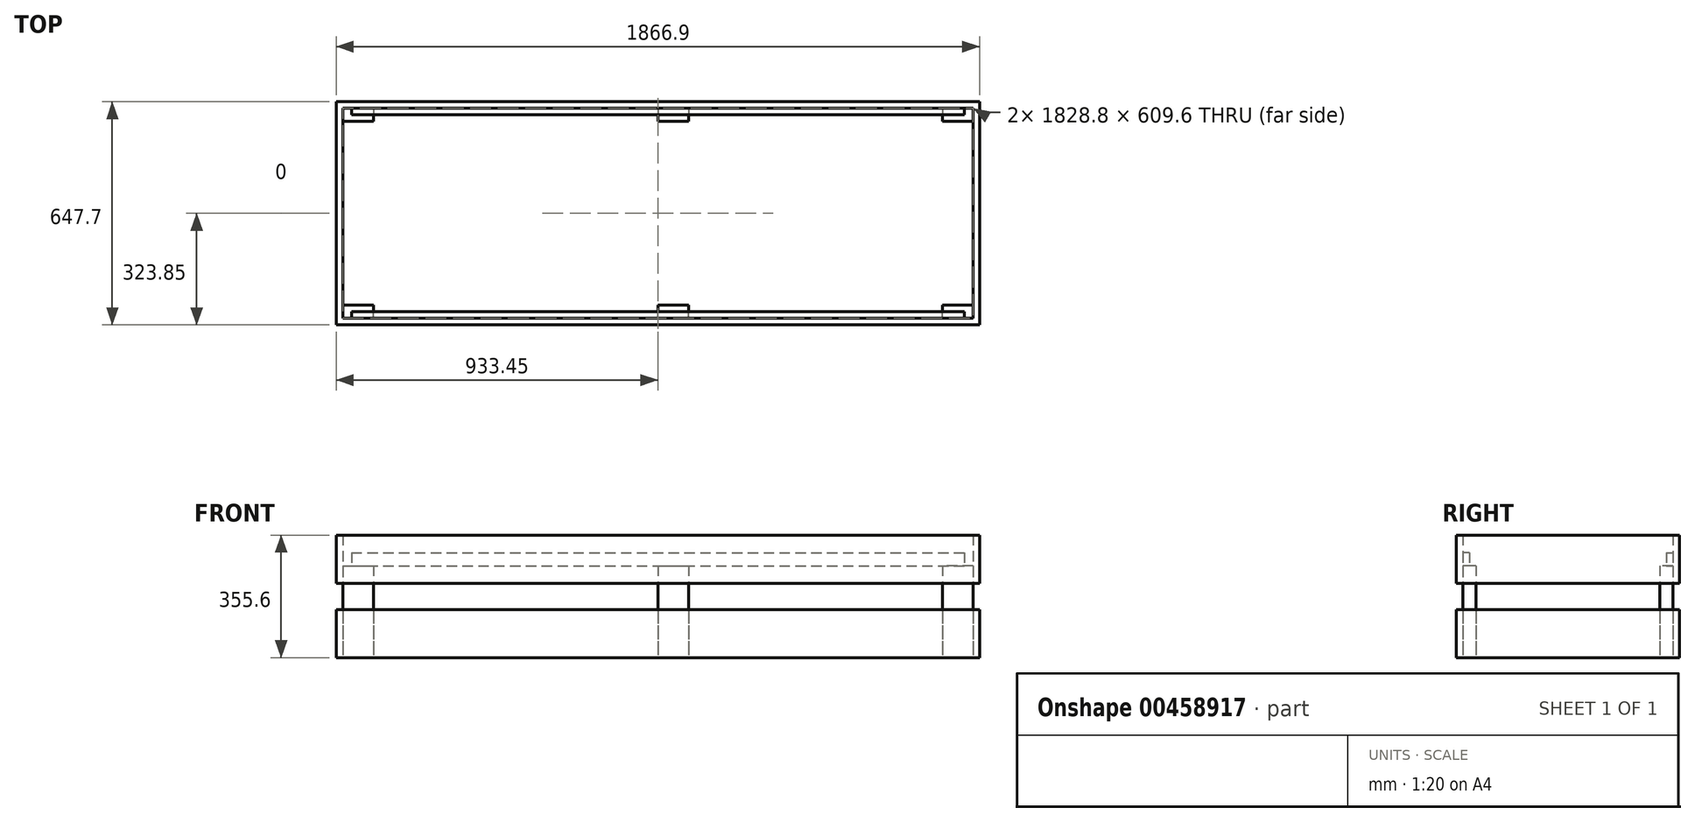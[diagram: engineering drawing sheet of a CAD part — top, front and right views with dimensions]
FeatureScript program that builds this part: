
annotation { "Feature Type Name" : "Feature", "Feature Type Description" : "" }
export const myFeature = defineFeature(function(context is Context, id is Id, definition is map)
    precondition{}
    {
        {
            var Q0;
            Q0=qCreatedBy(makeId("Top.planeOp"),FACE);
            var sketch = newSketch(context, id + "F0", { "sketchPlane" : qUnion([Q0])});
            skLineSegment(sketch, "E0.bottom", {"start": v(-933.45, 323.85) * mm, "end": v(933.45, 323.85) * mm});
            skLineSegment(sketch, "E0.top", {"start": v(-933.45, -323.85) * mm, "end": v(933.45, -323.85) * mm});
            skLineSegment(sketch, "E0.left", {"start": v(-933.45, 323.85) * mm, "end": v(-933.45, -323.85) * mm});
            skLineSegment(sketch, "E0.right", {"start": v(933.45, 323.85) * mm, "end": v(933.45, -323.85) * mm});
            skLineSegment(sketch, "E1", {"start": v(-933.45, 323.85) * mm, "end": v(933.45, -323.85) * mm, "construction": true});
            skSolve(sketch);
        }
        {
            var Q0;
            Q0=makeQuery(id+"F0.imprint","IMPRINT",FACE,{"disambiguationData":[TD([[makeQuery(id+"F0.imprint","IMPRINT",EDGE,{"derivedFrom":sQuery(id+"F0.wireOp",EDGE,"E0.bottom")}),-1.0]])]});
            extrude(context, id + "F1", {"entities" : qUnion([Q0]), "depth" : 355.6 * mm});
        }
        {
            var Q0;
            Q0=makeQuery(id+"F1.opExtrude","CAP_FACE",FACE,{"disambiguationData":[OSD([sQuery(id+"F0.wireOp",EDGE,"E0.bottom"),sQuery(id+"F0.wireOp",EDGE,"E0.top"),sQuery(id+"F0.wireOp",EDGE,"E0.left"),sQuery(id+"F0.wireOp",EDGE,"E0.right")])],"isStart":false});
            var Q1;
            Q1=makeQuery(id+"F1.opExtrude","CAP_FACE",FACE,{"disambiguationData":[OSD([sQuery(id+"F0.wireOp",EDGE,"E0.bottom"),sQuery(id+"F0.wireOp",EDGE,"E0.top"),sQuery(id+"F0.wireOp",EDGE,"E0.left"),sQuery(id+"F0.wireOp",EDGE,"E0.right")])],"isStart":true});
            shell(context, id + "F2", {"entities" : qUnion([Q0, Q1]), "thickness" : 19.05 * mm});
        }
        {
            var Q0;
            Q0=makeQuery(id+"F2.opShell","OFFSET_FACE",FACE,{"disambiguationData":[OSD([sQuery(id+"F0.wireOp",EDGE,"E0.bottom")])]});
            var sketch = newSketch(context, id + "F3", { "sketchPlane" : qUnion([Q0])});
            skLineSegment(sketch, "E2.bottom", {"start": v(-889, 304.8) * mm, "end": v(889, 304.8) * mm});
            skLineSegment(sketch, "E2.top", {"start": v(-889, 266.7) * mm, "end": v(889, 266.7) * mm});
            skLineSegment(sketch, "E2.left", {"start": v(-889, 304.8) * mm, "end": v(-889, 266.7) * mm});
            skLineSegment(sketch, "E2.right", {"start": v(889, 304.8) * mm, "end": v(889, 266.7) * mm});
            skSolve(sketch);
        }
        {
            var Q0;
            Q0=makeQuery(id+"F3.imprint","IMPRINT",FACE,{"disambiguationData":[TD([[makeQuery(id+"F3.imprint","IMPRINT",EDGE,{"derivedFrom":sQuery(id+"F3.wireOp",EDGE,"E2.bottom")}),-1.0]])]});
            extrude(context, id + "F4", {"entities" : qUnion([Q0]), "depth" : 19.05 * mm});
        }
        {
            var Q0;
            Q0=makeQuery(id+"F2.opShell","OFFSET_FACE",FACE,{"disambiguationData":[OSD([sQuery(id+"F0.wireOp",EDGE,"E0.top")])]});
            var sketch = newSketch(context, id + "F5", { "sketchPlane" : qUnion([Q0])});
            skLineSegment(sketch, "E3.bottom", {"start": v(-889, 304.8) * mm, "end": v(889, 304.8) * mm});
            skLineSegment(sketch, "E3.top", {"start": v(-889, 266.7) * mm, "end": v(889, 266.7) * mm});
            skLineSegment(sketch, "E3.left", {"start": v(-889, 304.8) * mm, "end": v(-889, 266.7) * mm});
            skLineSegment(sketch, "E3.right", {"start": v(889, 304.8) * mm, "end": v(889, 266.7) * mm});
            skSolve(sketch);
        }
        {
            var Q0;
            Q0 = qSketchRegion(id + "F5", true);
            extrude(context, id + "F6", {"entities" : qUnion([Q0]), "operationType" : NewBodyOperationType.ADD, "depth" : 19.05 * mm});
        }
        {
            var Q0;
            Q0=makeQuery(id+"F1.opExtrude","SWEPT_FACE",FACE,{"disambiguationData":[OSD([sQuery(id+"F0.wireOp",EDGE,"E0.top")])]});
            var sketch = newSketch(context, id + "F7", { "sketchPlane" : qUnion([Q0])});
            skLineSegment(sketch, "E4.bottom", {"start": v(-933.45, 215.9) * mm, "end": v(933.45, 215.9) * mm});
            skLineSegment(sketch, "E4.top", {"start": v(-933.45, 139.7) * mm, "end": v(933.45, 139.7) * mm});
            skLineSegment(sketch, "E4.left", {"start": v(-933.45, 215.9) * mm, "end": v(-933.45, 139.7) * mm});
            skLineSegment(sketch, "E4.right", {"start": v(933.45, 215.9) * mm, "end": v(933.45, 139.7) * mm});
            skSolve(sketch);
        }
        {
            var Q0;
            Q0=makeQuery(id+"F7.imprint","IMPRINT",FACE,{"disambiguationData":[TD([[makeQuery(id+"F7.imprint","IMPRINT",EDGE,{"derivedFrom":sQuery(id+"F7.wireOp",EDGE,"E4.bottom")}),-1.0]])]});
            extrude(context, id + "F8", {"entities" : qUnion([Q0]), "operationType" : NewBodyOperationType.REMOVE, "endBound" : BoundingType.THROUGH_ALL, "oppositeDirection" : true, "depth" : 25.4 * mm});
        }
        {
            var Q0;
            Q0=makeQuery(id+"F1.opExtrude","CAP_FACE",FACE,{"disambiguationData":[OSD([sQuery(id+"F0.wireOp",EDGE,"E0.bottom"),sQuery(id+"F0.wireOp",EDGE,"E0.top"),sQuery(id+"F0.wireOp",EDGE,"E0.left"),sQuery(id+"F0.wireOp",EDGE,"E0.right")])],"isStart":true});
            var sketch = newSketch(context, id + "F9", { "sketchPlane" : qUnion([Q0])});
            skLineSegment(sketch, "E5.bottom", {"start": v(914.4, -304.8) * mm, "end": v(825.5, -304.8) * mm});
            skLineSegment(sketch, "E5.top", {"start": v(914.4, -266.7) * mm, "end": v(825.5, -266.7) * mm});
            skLineSegment(sketch, "E5.left", {"start": v(914.4, -304.8) * mm, "end": v(914.4, -266.7) * mm});
            skLineSegment(sketch, "E5.right", {"start": v(825.5, -304.8) * mm, "end": v(825.5, -266.7) * mm});
            skLineSegment(sketch, "E6.bottom", {"start": v(914.4, 304.8) * mm, "end": v(825.5, 304.8) * mm});
            skLineSegment(sketch, "E6.top", {"start": v(914.4, 266.7) * mm, "end": v(825.5, 266.7) * mm});
            skLineSegment(sketch, "E6.left", {"start": v(914.4, 304.8) * mm, "end": v(914.4, 266.7) * mm});
            skLineSegment(sketch, "E6.right", {"start": v(825.5, 304.8) * mm, "end": v(825.5, 266.7) * mm});
            skLineSegment(sketch, "E7.bottom", {"start": v(-914.4, -304.8) * mm, "end": v(-825.5, -304.8) * mm});
            skLineSegment(sketch, "E7.top", {"start": v(-914.4, -266.7) * mm, "end": v(-825.5, -266.7) * mm});
            skLineSegment(sketch, "E7.left", {"start": v(-914.4, -304.8) * mm, "end": v(-914.4, -266.7) * mm});
            skLineSegment(sketch, "E7.right", {"start": v(-825.5, -304.8) * mm, "end": v(-825.5, -266.7) * mm});
            skLineSegment(sketch, "E8.bottom", {"start": v(-914.4, 304.8) * mm, "end": v(-825.5, 304.8) * mm});
            skLineSegment(sketch, "E8.top", {"start": v(-914.4, 266.7) * mm, "end": v(-825.5, 266.7) * mm});
            skLineSegment(sketch, "E8.left", {"start": v(-914.4, 304.8) * mm, "end": v(-914.4, 266.7) * mm});
            skLineSegment(sketch, "E8.right", {"start": v(-825.5, 304.8) * mm, "end": v(-825.5, 266.7) * mm});
            skLineSegment(sketch, "E9.bottom", {"start": v(88.9, 304.8) * mm, "end": v(0, 304.8) * mm});
            skLineSegment(sketch, "E9.top", {"start": v(88.9, 266.7) * mm, "end": v(0, 266.7) * mm});
            skLineSegment(sketch, "E9.left", {"start": v(88.9, 304.8) * mm, "end": v(88.9, 266.7) * mm});
            skLineSegment(sketch, "E9.right", {"start": v(0, 304.8) * mm, "end": v(0, 266.7) * mm});
            skLineSegment(sketch, "E10.bottom", {"start": v(88.9, -304.8) * mm, "end": v(0, -304.8) * mm});
            skLineSegment(sketch, "E10.top", {"start": v(88.9, -266.7) * mm, "end": v(0, -266.7) * mm});
            skLineSegment(sketch, "E10.left", {"start": v(88.9, -304.8) * mm, "end": v(88.9, -266.7) * mm});
            skLineSegment(sketch, "E10.right", {"start": v(0, -304.8) * mm, "end": v(0, -266.7) * mm});
            skSolve(sketch);
        }
        {
            var Q0;
            Q0=makeQuery(id+"F9.imprint","IMPRINT",FACE,{"disambiguationData":[TD([[makeQuery(id+"F9.imprint","IMPRINT",EDGE,{"derivedFrom":sQuery(id+"F9.wireOp",EDGE,"E8.bottom")}),-1.0]])]});
            var Q1;
            Q1=makeQuery(id+"F9.imprint","IMPRINT",FACE,{"disambiguationData":[TD([[makeQuery(id+"F9.imprint","IMPRINT",EDGE,{"derivedFrom":sQuery(id+"F9.wireOp",EDGE,"E7.bottom")}),1.0]])]});
            var Q2;
            Q2=makeQuery(id+"F9.imprint","IMPRINT",FACE,{"disambiguationData":[TD([[makeQuery(id+"F9.imprint","IMPRINT",EDGE,{"derivedFrom":sQuery(id+"F9.wireOp",EDGE,"E9.bottom")}),-1.0]])]});
            var Q3;
            Q3=makeQuery(id+"F9.imprint","IMPRINT",FACE,{"disambiguationData":[TD([[makeQuery(id+"F9.imprint","IMPRINT",EDGE,{"derivedFrom":sQuery(id+"F9.wireOp",EDGE,"E10.bottom")}),1.0]])]});
            var Q4;
            Q4=makeQuery(id+"F9.imprint","IMPRINT",FACE,{"disambiguationData":[TD([[makeQuery(id+"F9.imprint","IMPRINT",EDGE,{"derivedFrom":sQuery(id+"F9.wireOp",EDGE,"E5.bottom")}),1.0]])]});
            var Q5;
            Q5=makeQuery(id+"F9.imprint","IMPRINT",FACE,{"disambiguationData":[TD([[makeQuery(id+"F9.imprint","IMPRINT",EDGE,{"derivedFrom":sQuery(id+"F9.wireOp",EDGE,"E6.bottom")}),-1.0]])]});
            var Q6;
            Q6=makeQuery(id+"F6.opExtrude","SWEPT_FACE",FACE,{"disambiguationData":[OSD([sQuery(id+"F5.wireOp",EDGE,"E3.top")])]});
            extrude(context, id + "F10", {"entities" : qUnion([Q0, Q1, Q2, Q3, Q4, Q5]), "endBound" : BoundingType.UP_TO_SURFACE, "oppositeDirection" : true, "endBoundEntityFace" : qUnion([Q6]), "depth" : 25.4 * mm});
        }
    });
